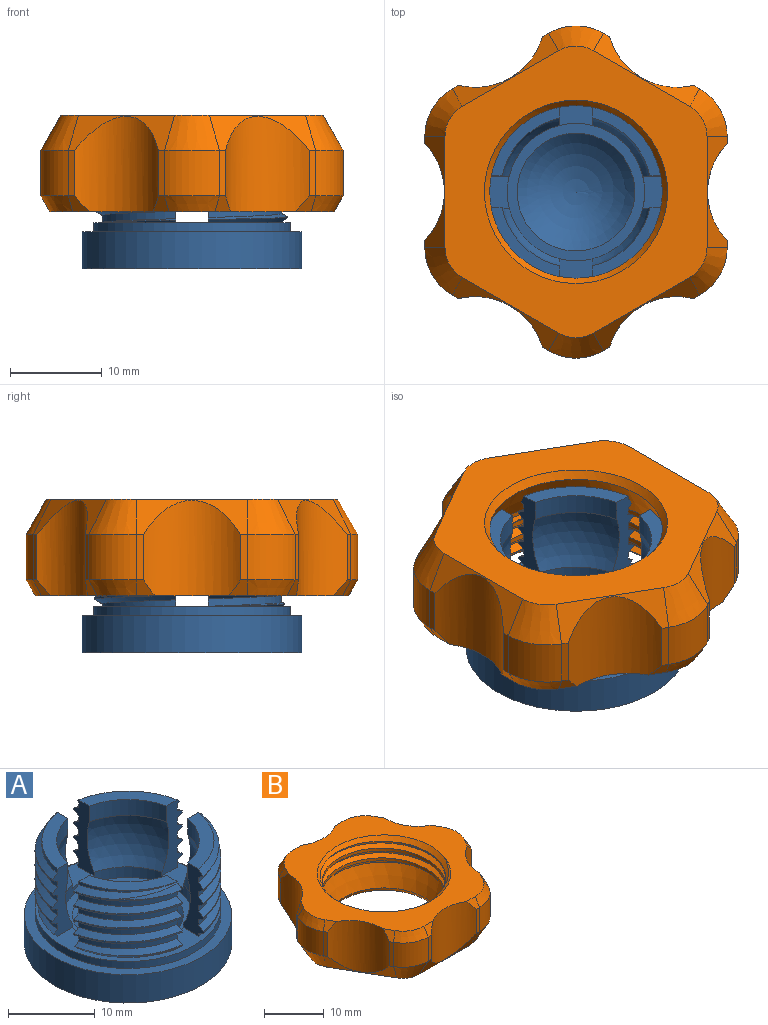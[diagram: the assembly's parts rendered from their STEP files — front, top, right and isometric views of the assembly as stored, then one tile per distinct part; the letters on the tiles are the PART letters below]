
ASSEMBLY  parts=2 mates=1
PART A: 112 faces, bbox 24x24.8x15.3 mm
  f0: cylinder r=10.75mm len=8.86mm, axis (0,0,-1), area 2.7mm2, adj f28,f48,f105,f107
  f1: cylinder r=10.75mm len=8.86mm, axis (0,0,-1), area 2.7mm2, adj f27,f47,f105,f107
  f2: cylinder r=10.75mm len=8.86mm, axis (0,0,-1), area 2.7mm2, adj f26,f46,f105,f107
  f3: cylinder r=10.75mm len=8.86mm, axis (0,0,-1), area 2.7mm2, adj f25,f45,f105,f107
  f4: cylinder r=10.75mm len=8.86mm, axis (0,0,-1), area 2.7mm2, adj f33,f52,f103,f104
  f5: cylinder r=10.75mm len=8.86mm, axis (0,0,-1), area 2.7mm2, adj f32,f51,f103,f104
  f6: cylinder r=10.75mm len=8.86mm, axis (0,0,-1), area 2.7mm2, adj f31,f50,f103,f104
  f7: cylinder r=10.75mm len=8.51mm, axis (0,0,-1), area 1.7mm2, adj f23,f30,f49,f104
  f8: cylinder r=10.75mm len=8.86mm, axis (0,0,-1), area 2.7mm2, adj f36,f54,f101,f106
  f9: cylinder r=10.75mm len=8.86mm, axis (0,0,-1), area 2.7mm2, adj f37,f55,f101,f106
  f10: cylinder r=10.75mm len=8.86mm, axis (0,0,-1), area 2.7mm2, adj f38,f56,f101,f106
  f11: cylinder r=10.75mm len=4.63mm, axis (0,0,-1), area 0.4mm2, adj f20,f34,f103
  f12: cylinder r=10.75mm len=8.86mm, axis (0,0,-1), area 2.7mm2, adj f40,f59,f100,f102
  f13: cylinder r=10.75mm len=8.86mm, axis (0,0,-1), area 2.7mm2, adj f41,f60,f100,f102
  f14: cylinder r=10.75mm len=8.86mm, axis (0,0,-1), area 2.7mm2, adj f42,f61,f100,f102
  f15: cylinder r=10.75mm len=8.86mm, axis (0,0,-1), area 2.7mm2, adj f43,f62,f100,f102
  f16: plane 8.05x8.05mm, normal (0,0,1), area 18.3mm2, adj f22,f67,f105,f107,f108
  f17: plane 8.05x8.05mm, normal (0,0,1), area 18.3mm2, adj f72,f103,f104,f110
  f18: plane 8.05x8.05mm, normal (0,0,1), area 18.3mm2, adj f90,f101,f106,f109
  f19: cone r=10.75mm half-angle=45deg, axis (0,0,1), area 8.2mm2, adj f29,f92,f105,f107
  f20: cone r=10.75mm half-angle=45deg, axis (0,0,1), area 9.9mm2, adj f11,f34,f57,f92,f103,f104
  f21: cone r=10.75mm half-angle=45deg, axis (0,0,1), area 2.7mm2, adj f39,f92,f101,f106
  f22: cone r=9.95mm half-angle=45deg, axis (0,0,-1), area 0.3mm2, adj f16,f44,f107
  f23: cone r=9.95mm half-angle=45deg, axis (0,0,-1), area 3.7mm2, adj f7,f30,f49,f103
  f24: cone r=9.95mm half-angle=45deg, axis (0,0,-1), area 10.4mm2, adj f58,f89,f100,f102
  f25: bspline ~16.13x12.41mm, area 12mm2, adj f3,f67,f105,f107
  f26: bspline ~16.13x12.41mm, area 12mm2, adj f2,f66,f105,f107
  f27: bspline ~16.13x12.41mm, area 12mm2, adj f1,f65,f105,f107
  f28: bspline ~16.13x12.41mm, area 12mm2, adj f0,f64,f105,f107
  f29: bspline ~16.13x12.41mm, area 6.8mm2, adj f19,f63,f105,f107
  f30: bspline ~16.13x12.41mm, area 8.9mm2, adj f7,f23,f72,f103,f104
  f31: bspline ~16.13x12.41mm, area 12mm2, adj f6,f71,f103,f104
  f32: bspline ~16.13x12.41mm, area 12mm2, adj f5,f70,f103,f104
  f33: bspline ~16.13x12.41mm, area 12mm2, adj f4,f69,f103,f104
  f34: bspline ~16.13x12.41mm, area 11.3mm2, adj f11,f20,f68,f103,f104
  f35: bspline ~16.13x12.41mm, area 12mm2, adj f73,f88,f101,f106
  f36: bspline ~16.13x12.41mm, area 12mm2, adj f8,f74,f101,f106
  f37: bspline ~16.13x12.41mm, area 12mm2, adj f9,f75,f101,f106
  f38: bspline ~16.13x12.41mm, area 12mm2, adj f10,f76,f101,f106
  f39: bspline ~16.13x12.41mm, area 2.2mm2, adj f21,f77,f101,f106
  f40: bspline ~16.13x12.41mm, area 12mm2, adj f12,f79,f100,f102
  f41: bspline ~16.13x12.41mm, area 12mm2, adj f13,f80,f100,f102
  f42: bspline ~16.13x12.41mm, area 12mm2, adj f14,f81,f100,f102
  f43: bspline ~16.13x12.41mm, area 12mm2, adj f15,f82,f100,f102
  f44: bspline ~16.13x12.41mm, area 0.2mm2, adj f22,f67,f107
  f45: bspline ~16.13x12.41mm, area 12mm2, adj f3,f66,f105,f107
  f46: bspline ~16.13x12.41mm, area 12mm2, adj f2,f65,f105,f107
  f47: bspline ~16.13x12.41mm, area 12mm2, adj f1,f64,f105,f107
  f48: bspline ~16.13x12.41mm, area 12mm2, adj f0,f63,f105,f107
  f49: bspline ~16.13x12.41mm, area 12mm2, adj f7,f23,f71,f103,f104
  f50: bspline ~16.13x12.41mm, area 12mm2, adj f6,f70,f103,f104
  f51: bspline ~16.13x12.41mm, area 12mm2, adj f5,f69,f103,f104
  f52: bspline ~16.13x12.41mm, area 12mm2, adj f4,f68,f103,f104
  f53: bspline ~16.13x12.41mm, area 12mm2, adj f74,f88,f101,f106
  f54: bspline ~16.13x12.41mm, area 12mm2, adj f8,f75,f101,f106
  f55: bspline ~16.13x12.41mm, area 12mm2, adj f9,f76,f101,f106
  f56: bspline ~16.13x12.41mm, area 12mm2, adj f10,f77,f101,f106
  f57: bspline ~16.13x12.41mm, area 3mm2, adj f20,f78,f103
  f58: bspline ~16.13x12.41mm, area 8.6mm2, adj f24,f79,f100,f102
  f59: bspline ~16.13x12.41mm, area 12mm2, adj f12,f80,f100,f102
  f60: bspline ~16.13x12.41mm, area 12mm2, adj f13,f81,f100,f102
  f61: bspline ~16.13x12.41mm, area 12mm2, adj f14,f82,f100,f102
  f62: bspline ~16.13x12.41mm, area 12mm2, adj f15,f83,f100,f102
  f63: cylinder r=9.95mm len=8.05mm, axis (0,0,-1), area 9.7mm2, adj f29,f48,f105,f107
  f64: cylinder r=9.95mm len=8.05mm, axis (0,0,-1), area 9.7mm2, adj f28,f47,f105,f107
  f65: cylinder r=9.95mm len=8.05mm, axis (0,0,-1), area 9.7mm2, adj f27,f46,f105,f107
  f66: cylinder r=9.95mm len=8.05mm, axis (0,0,-1), area 9.7mm2, adj f26,f45,f105,f107
  f67: cylinder r=9.95mm len=8.05mm, axis (0,0,-1), area 8.7mm2, adj f16,f25,f44,f105,f107
  f68: cylinder r=9.95mm len=8.05mm, axis (0,0,-1), area 9.7mm2, adj f34,f52,f103,f104
  f69: cylinder r=9.95mm len=8.05mm, axis (0,0,-1), area 9.7mm2, adj f33,f51,f103,f104
  f70: cylinder r=9.95mm len=8.05mm, axis (0,0,-1), area 9.7mm2, adj f32,f50,f103,f104
  f71: cylinder r=9.95mm len=8.05mm, axis (0,0,-1), area 9.7mm2, adj f31,f49,f103,f104
  f72: cylinder r=9.95mm len=8.05mm, axis (0,0,-1), area 3mm2, adj f17,f30,f103,f104
  f73: cylinder r=9.95mm len=8.05mm, axis (0,0,-1), area 9.7mm2, adj f35,f91,f101,f106
  f74: cylinder r=9.95mm len=8.05mm, axis (0,0,-1), area 9.7mm2, adj f36,f53,f101,f106
  f75: cylinder r=9.95mm len=8.05mm, axis (0,0,-1), area 9.7mm2, adj f37,f54,f101,f106
  f76: cylinder r=9.95mm len=8.05mm, axis (0,0,-1), area 9.7mm2, adj f38,f55,f101,f106
  f77: cylinder r=9.95mm len=8.05mm, axis (0,0,-1), area 9.7mm2, adj f39,f56,f101,f106
  f78: cylinder r=9.95mm len=6.33mm, axis (0,0,-1), area 0.9mm2, adj f57,f92,f103
  f79: cylinder r=9.95mm len=8.05mm, axis (0,0,-1), area 9.7mm2, adj f40,f58,f100,f102
  f80: cylinder r=9.95mm len=8.05mm, axis (0,0,-1), area 9.7mm2, adj f41,f59,f100,f102
  f81: cylinder r=9.95mm len=8.05mm, axis (0,0,-1), area 9.7mm2, adj f42,f60,f100,f102
  f82: cylinder r=9.95mm len=8.05mm, axis (0,0,-1), area 9.7mm2, adj f43,f61,f100,f102
  f83: cylinder r=9.95mm len=8.05mm, axis (0,0,-1), area 6.7mm2, adj f62,f92,f100,f102
  f84: sphere r=8.62mm, area 66.8mm2, adj f87,f105,f107,f108
  f85: sphere r=8.62mm, area 66.8mm2, adj f87,f103,f104,f110
  f86: sphere r=8.62mm, area 66.8mm2, adj f87,f101,f106,f109
  f87: cylinder r=7.5mm len=15mm, axis (0,0,-1), area 63.7mm2, adj f84,f85,f86,f92,f97,f98,f100,f101
  f88: cylinder r=10.75mm len=8.86mm, axis (0,0,-1), area 2.7mm2, adj f35,f53,f101,f106
  f89: plane 8.05x8.05mm, normal (0,0,1), area 18.3mm2, adj f24,f100,f102,f111
  f90: cone r=9.95mm half-angle=45deg, axis (0,0,-1), area 4.9mm2, adj f18,f91,f101,f106
  f91: bspline ~16.13x12.41mm, area 4mm2, adj f73,f90,f101,f106
  f92: plane 21.5x21.5mm, normal (0,0,1), area 86.6mm2, adj f19,f20,f21,f78,f83,f87,f93,f100
  f93: cylinder r=10.75mm len=21.5mm, axis (0,0,1), area 67.5mm2, adj f92,f94
  f94: plane 24x24mm, normal (0,0,1), area 89.3mm2, adj f93,f95
  f95: cylinder r=12mm len=24mm, axis (0,0,1), area 301.6mm2, adj f94,f96
  f96: plane 24x24mm, normal (0,0,-1), area 452.4mm2, adj f95
  f97: sphere r=8.62mm, area 66.8mm2, adj f87,f100,f102,f111
  f98: plane 15x15mm, normal (0,0,1), area 47.1mm2, adj f87,f99
  f99: sphere r=8.62mm, area 155.4mm2, adj f98
  f100: plane 9.51x3.32mm, normal (0,1,0), area 18.6mm2, adj f12,f13,f14,f15,f24,f40,f41,f42
  f101: plane 9.51x3.32mm, normal (0,-1,0), area 18.6mm2, adj f8,f9,f10,f18,f21,f35,f36,f37
  f102: plane 9.51x3.32mm, normal (-1,0,0), area 18.9mm2, adj f12,f13,f14,f15,f24,f40,f41,f42
  f103: plane 9.51x3.32mm, normal (1,0,0), area 18.9mm2, adj f4,f5,f6,f11,f17,f20,f23,f30
  f104: plane 9.51x3.32mm, normal (0,1,0), area 18.8mm2, adj f4,f5,f6,f7,f17,f20,f30,f31
  f105: plane 9.51x3.32mm, normal (0,-1,0), area 18.7mm2, adj f0,f1,f2,f3,f16,f19,f25,f26
  f106: plane 9.51x3.32mm, normal (-1,0,0), area 18.5mm2, adj f8,f9,f10,f18,f21,f35,f36,f37
  f107: plane 9.51x3.32mm, normal (1,0,0), area 18.6mm2, adj f0,f1,f2,f3,f16,f19,f22,f25
  f108: cylinder r=8.25mm len=6.31mm, axis (0,0,1), area 21.2mm2, adj f16,f84,f105,f107
  f109: cylinder r=8.25mm len=6.31mm, axis (0,0,1), area 21.2mm2, adj f18,f86,f101,f106
  f110: cylinder r=8.25mm len=6.31mm, axis (0,0,1), area 21.2mm2, adj f17,f85,f103,f104
  f111: cylinder r=8.25mm len=6.31mm, axis (0,0,1), area 21.2mm2, adj f89,f97,f100,f102
PART B: 66 faces, bbox 36.6x33.4x11.6 mm
  f0: cylinder r=11.15mm len=22.3mm, axis (0,0,1), area 55.7mm2, adj f2,f23,f24,f27,f34
  f1: cylinder r=11.15mm len=22.3mm, axis (0,0,1), area 25.1mm2, adj f2,f22,f23,f24
  f2: cylinder r=11.15mm len=22.3mm, axis (0,0,1), area 28mm2, adj f0,f1,f23,f24
  f3: cylinder r=7.62mm len=10.4mm, axis (0,0,-1), area 104.1mm2, adj f4,f21,f22,f39,f44,f61
  f4: plane 4.96x0.67mm, normal (0.87,-0.5,0), area 3.8mm2, adj f3,f28,f44,f61
  f5: plane 4.96x0.67mm, normal (0.87,0.5,0), area 3.8mm2, adj f6,f28,f42,f57
  f6: cylinder r=7.62mm len=10.4mm, axis (0,0,-1), area 104.1mm2, adj f5,f7,f22,f42,f47,f57
  f7: plane 4.96x0.67mm, normal (0.87,0.5,0), area 3.8mm2, adj f6,f29,f47,f57
  f8: plane 4.96x0.77mm, normal (0,1,0), area 3.8mm2, adj f9,f29,f45,f54
  f9: cylinder r=7.62mm len=10.59mm, axis (0,0,-1), area 104.1mm2, adj f8,f10,f22,f45,f50,f54
  f10: plane 4.96x0.77mm, normal (0,1,0), area 3.8mm2, adj f9,f30,f50,f54
  f11: plane 4.96x0.67mm, normal (-0.87,0.5,0), area 3.8mm2, adj f12,f30,f48,f58
  f12: cylinder r=7.62mm len=10.4mm, axis (0,0,-1), area 104.1mm2, adj f11,f13,f22,f48,f53,f58
  f13: plane 4.96x0.67mm, normal (-0.87,0.5,0), area 3.8mm2, adj f12,f31,f53,f58
  f14: plane 4.96x0.67mm, normal (-0.87,-0.5,0), area 3.8mm2, adj f15,f31,f51,f62
  f15: cylinder r=7.62mm len=10.4mm, axis (0,0,-1), area 104.1mm2, adj f14,f16,f22,f38,f51,f62
  f16: plane 4.96x0.67mm, normal (-0.87,-0.5,0), area 3.8mm2, adj f15,f32,f38,f62
  f17: plane 4.96x0.77mm, normal (0,-1,0), area 3.8mm2, adj f18,f32,f36,f65
  f18: cylinder r=7.62mm len=10.59mm, axis (0,0,-1), area 104.1mm2, adj f17,f19,f22,f36,f41,f65
  f19: plane 4.96x0.77mm, normal (0,-1,0), area 3.8mm2, adj f18,f33,f41,f65
  f20: cylinder r=10.35mm len=20.7mm, axis (0,0,-1), area 81.9mm2, adj f23,f24,f25,f27
  f21: plane 4.96x0.67mm, normal (0.87,-0.5,0), area 3.8mm2, adj f3,f33,f39,f61
  f22: plane 34.25x31mm, normal (0,0,1), area 396.6mm2, adj f1,f3,f6,f9,f12,f15,f18,f25
  f23: bspline ~25.75x22.3mm, area 146.6mm2, adj f0,f1,f2,f20,f25,f27
  f24: bspline ~25.75x22.3mm, area 146.7mm2, adj f0,f1,f2,f20,f25,f27
  f25: cone r=10.35mm half-angle=45deg, axis (0,0,1), area 42.3mm2, adj f20,f22,f23,f24
  f26: plane 31.85x28.6mm, normal (0,0,-1), area 389.9mm2, adj f35,f54,f55,f56,f57,f58,f59,f60
  f27: plane 22.7x22.7mm, normal (0,0,-1), area 29.9mm2, adj f0,f20,f23,f24
  f28: cylinder r=6mm len=6mm, axis (0,0,-1), area 31.1mm2, adj f4,f5,f43,f59
  f29: cylinder r=6mm len=5.2mm, axis (0,0,-1), area 31.1mm2, adj f7,f8,f46,f55
  f30: cylinder r=6mm len=5.2mm, axis (0,0,-1), area 31.1mm2, adj f10,f11,f49,f56
  f31: cylinder r=6mm len=6mm, axis (0,0,-1), area 31.1mm2, adj f13,f14,f52,f60
  f32: cylinder r=6mm len=5.2mm, axis (0,0,-1), area 31.1mm2, adj f16,f17,f37,f64
  f33: cylinder r=6mm len=5.2mm, axis (0,0,-1), area 31.1mm2, adj f19,f21,f40,f63
  f34: cone r=9.9mm half-angle=23deg, axis (0,0,1), area 286.1mm2, adj f0,f35
  f35: cone r=10mm half-angle=33.5deg, axis (0,0,-1), area 63.6mm2, adj f26,f34
  f36: plane 2.18x1.85mm, normal (0,-0.87,0.5), area 2.7mm2, adj f17,f18,f22,f37
  f37: cone r=5mm half-angle=30deg, axis (0,0,-1), area 11.5mm2, adj f22,f32,f36,f38
  f38: plane 2.4x1.85mm, normal (-0.75,-0.43,0.5), area 2.7mm2, adj f15,f16,f22,f37
  f39: plane 2.4x1.85mm, normal (0.75,-0.43,0.5), area 2.7mm2, adj f3,f21,f22,f40
  f40: cone r=5mm half-angle=30deg, axis (0,0,-1), area 11.5mm2, adj f22,f33,f39,f41
  f41: plane 2.18x1.85mm, normal (0,-0.87,0.5), area 2.7mm2, adj f18,f19,f22,f40
  f42: plane 2.01x1.9mm, normal (0.75,0.43,0.5), area 2.7mm2, adj f5,f6,f22,f43
  f43: cone r=5mm half-angle=30deg, axis (0,0,-1), area 11.5mm2, adj f22,f28,f42,f44
  f44: plane 2.01x1.9mm, normal (0.75,-0.43,0.5), area 2.7mm2, adj f3,f4,f22,f43
  f45: plane 2.18x1.85mm, normal (0,0.87,0.5), area 2.7mm2, adj f8,f9,f22,f46
  f46: cone r=5mm half-angle=30deg, axis (0,0,-1), area 11.5mm2, adj f22,f29,f45,f47
  f47: plane 2.4x1.85mm, normal (0.75,0.43,0.5), area 2.7mm2, adj f6,f7,f22,f46
  f48: plane 2.4x1.85mm, normal (-0.75,0.43,0.5), area 2.7mm2, adj f11,f12,f22,f49
  f49: cone r=5mm half-angle=30deg, axis (0,0,-1), area 11.5mm2, adj f22,f30,f48,f50
  f50: plane 2.18x1.85mm, normal (0,0.87,0.5), area 2.7mm2, adj f9,f10,f22,f49
  f51: plane 2.01x1.9mm, normal (-0.75,-0.43,0.5), area 2.7mm2, adj f14,f15,f22,f52
  f52: cone r=5mm half-angle=30deg, axis (0,0,-1), area 11.5mm2, adj f22,f31,f51,f53
  f53: plane 2.01x1.9mm, normal (-0.75,0.43,0.5), area 2.7mm2, adj f12,f13,f22,f52
  f54: plane 12.12x3.81mm, normal (0,0.87,-0.5), area 22.2mm2, adj f8,f9,f10,f26,f55,f56
  f55: cone r=3.8mm half-angle=30deg, axis (0,0,1), area 22.6mm2, adj f26,f29,f54,f57
  f56: cone r=3.8mm half-angle=30deg, axis (0,0,1), area 22.6mm2, adj f26,f30,f54,f58
  f57: plane 11.6x7.97mm, normal (0.75,0.43,-0.5), area 22.2mm2, adj f5,f6,f7,f26,f55,f59
  f58: plane 11.6x7.97mm, normal (-0.75,0.43,-0.5), area 22.2mm2, adj f11,f12,f13,f26,f56,f60
  f59: cone r=3.8mm half-angle=30deg, axis (0,0,1), area 22.6mm2, adj f26,f28,f57,f61
  f60: cone r=3.8mm half-angle=30deg, axis (0,0,1), area 22.6mm2, adj f26,f31,f58,f62
  f61: plane 11.6x7.97mm, normal (0.75,-0.43,-0.5), area 22.2mm2, adj f3,f4,f21,f26,f59,f63
  f62: plane 11.6x7.97mm, normal (-0.75,-0.43,-0.5), area 22.2mm2, adj f14,f15,f16,f26,f60,f64
  f63: cone r=3.8mm half-angle=30deg, axis (0,0,1), area 22.6mm2, adj f26,f33,f61,f65
  f64: cone r=3.8mm half-angle=30deg, axis (0,0,1), area 22.6mm2, adj f26,f32,f62,f65
  f65: plane 12.12x3.81mm, normal (0,-0.87,-0.5), area 22.2mm2, adj f17,f18,f19,f26,f63,f64
PLACE A rot(axis=(0,0,1),180deg) t=(0,0,9.75)mm
PLACE B rot(axis=(0.71,0.71,0),180deg) t=(0,0,11.2)mm
MATE revolute A.f87 <-> B.f20  axis (0,0,1) through (0,0,5)mm
